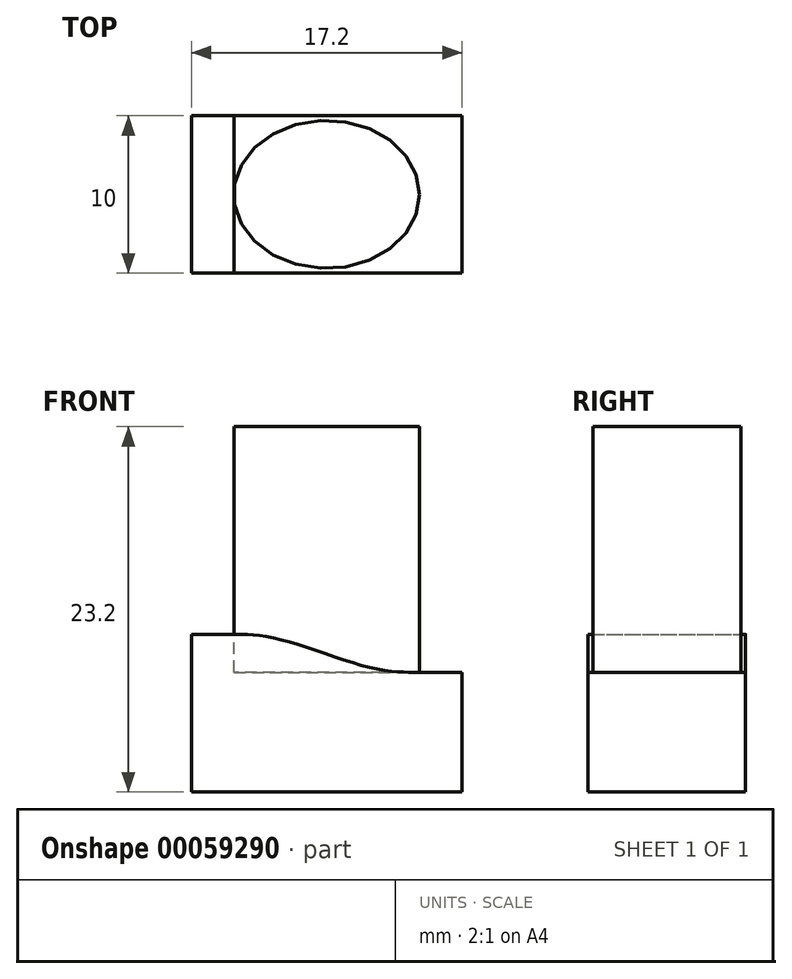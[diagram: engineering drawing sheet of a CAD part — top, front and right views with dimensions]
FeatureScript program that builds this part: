
annotation { "Feature Type Name" : "Feature", "Feature Type Description" : "" }
export const myFeature = defineFeature(function(context is Context, id is Id, definition is map)
    precondition{}
    {
        {
            var Q0;
            Q0=qCreatedBy(makeId("Top.planeOp"),FACE);
            var sketch = newSketch(context, id + "F0", { "sketchPlane" : qUnion([Q0])});
            skEllipse(sketch, "E0", {"center": v(0, 0) * mm, "majorRadius": 5.9 * mm, "minorRadius": 4.7 * mm, "majorAxis": v(1, 0)});
            skSolve(sketch);
        }
        {
            var Q0;
            Q0=makeQuery(id+"F0.imprint","IMPRINT",FACE,{"disambiguationData":[TD([[makeQuery(id+"F0.imprint","IMPRINT",EDGE,{"derivedFrom":sQuery(id+"F0.wireOp",EDGE,"E0")}),1.0]])]});
            extrude(context, id + "F1", {"entities" : qUnion([Q0]), "oppositeDirection" : true, "depth" : 15.6 * mm});
        }
        {
            var Q0;
            Q0=qCreatedBy(makeId("Front.planeOp"),FACE);
            var sketch = newSketch(context, id + "F2", { "sketchPlane" : qUnion([Q0])});
            skFitSpline(sketch, "E1", {"points": [v(5.9, -15.6) * mm, v(3.03, -15.37) * mm, v(-3.04, -13.5) * mm, v(-5.9, -13.2) * mm], "startDerivative": vector(-7.97, 0) * mm, "endDerivative": vector(-7.46, -0.33) * mm});
            skLineSegment(sketch, "E2", {"start": v(-5.9, -15.6) * mm, "end": v(-5.9, 0) * mm, "construction": true});
            skLineSegment(sketch, "E3", {"start": v(5.9, 0) * mm, "end": v(5.9, -15.6) * mm, "construction": true});
            skLineSegment(sketch, "E4.0", {"start": v(-5.9, -15.6) * mm, "end": v(5.9, -15.6) * mm, "construction": true});
            skLineSegment(sketch, "E5.bottom", {"start": v(-8.6, -13.2) * mm, "end": v(-5.05, -13.2) * mm});
            skLineSegment(sketch, "E5.top", {"start": v(-8.6, -23.2) * mm, "end": v(8.6, -23.2) * mm});
            skLineSegment(sketch, "E5.left", {"start": v(-8.6, -13.2) * mm, "end": v(-8.6, -23.2) * mm});
            skLineSegment(sketch, "E5.right", {"start": v(8.6, -15.6) * mm, "end": v(8.6, -23.2) * mm});
            skLineSegment(sketch, "E6", {"start": v(0, 0) * mm, "end": v(0, -25.67) * mm, "construction": true});
            skLineSegment(sketch, "E7", {"start": v(5.9, -15.6) * mm, "end": v(8.6, -15.6) * mm});
            skSolve(sketch);
        }
        {
            var Q0;
            Q0 = qSketchRegion(id + "F2", true);
            extrude(context, id + "F3", {"entities" : qUnion([Q0]), "endBound" : BoundingType.SYMMETRIC, "depth" : 10 * mm});
        }
    });
